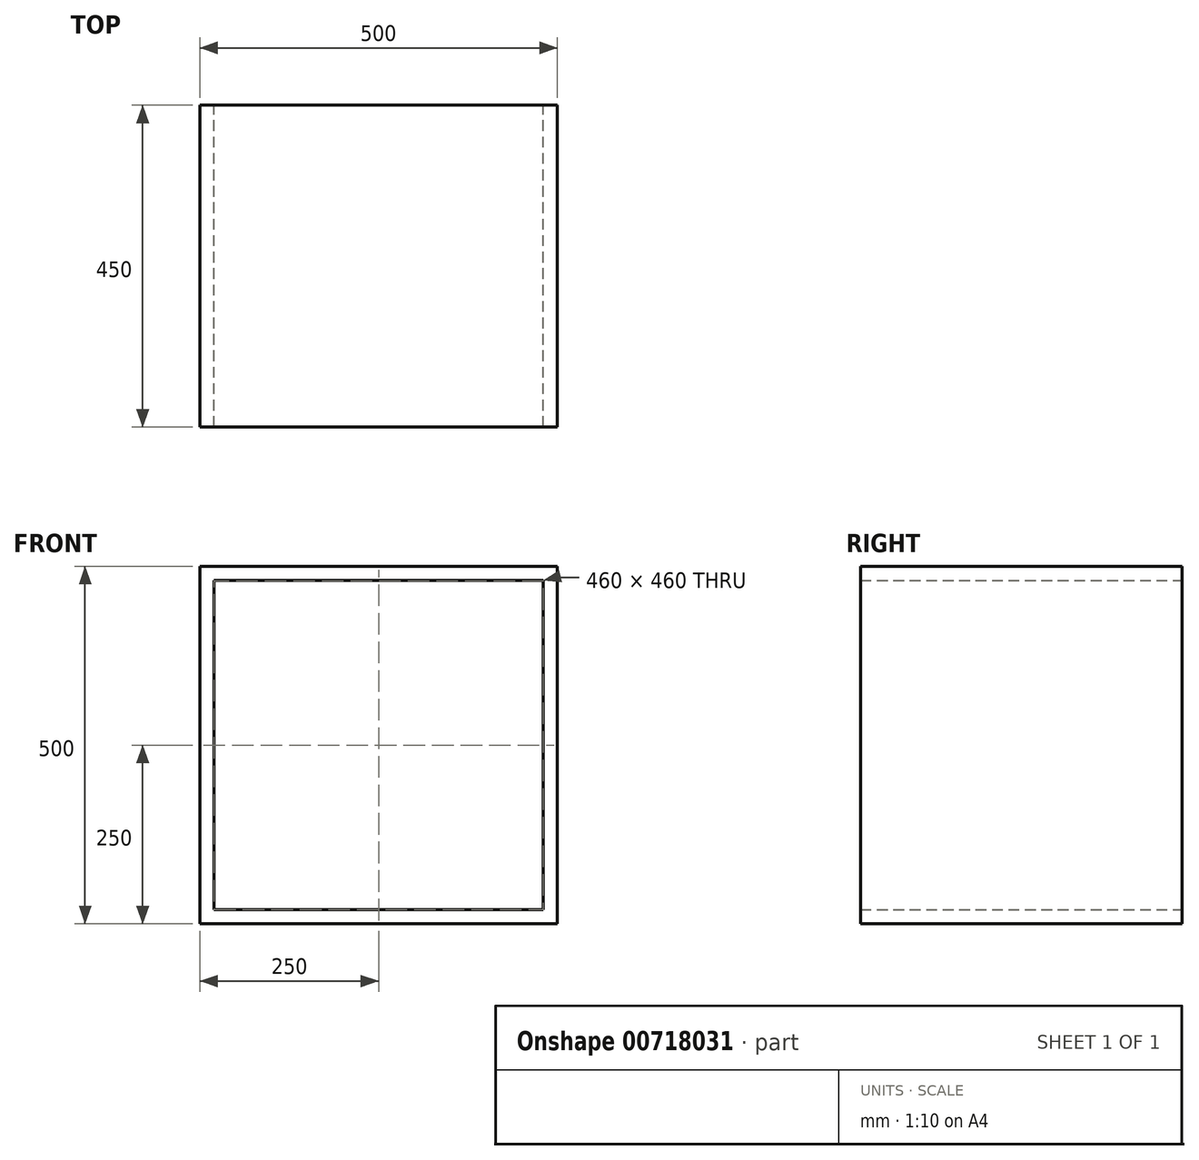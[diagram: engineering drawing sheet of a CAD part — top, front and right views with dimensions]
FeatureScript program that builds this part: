
annotation { "Feature Type Name" : "Feature", "Feature Type Description" : "" }
export const myFeature = defineFeature(function(context is Context, id is Id, definition is map)
    precondition{}
    {
        {
            var Q0;
            Q0=qCreatedBy(makeId("Front.planeOp"),FACE);
            var sketch = newSketch(context, id + "F0", { "sketchPlane" : qUnion([Q0])});
            skLineSegment(sketch, "E0.bottom", {"start": v(250, 250) * mm, "end": v(-250, 250) * mm});
            skLineSegment(sketch, "E0.top", {"start": v(250, -250) * mm, "end": v(-250, -250) * mm});
            skLineSegment(sketch, "E0.left", {"start": v(250, 250) * mm, "end": v(250, -250) * mm});
            skLineSegment(sketch, "E0.right", {"start": v(-250, 250) * mm, "end": v(-250, -250) * mm});
            skPoint(sketch, "E0.middle", {"position": v(0, 0) * mm});
            skLineSegment(sketch, "E1.0", {"start": v(-230, 230) * mm, "end": v(-230, -230) * mm});
            skLineSegment(sketch, "E1.1", {"start": v(230, 230) * mm, "end": v(-230, 230) * mm});
            skLineSegment(sketch, "E1.2", {"start": v(230, 230) * mm, "end": v(230, -230) * mm});
            skLineSegment(sketch, "E1.3", {"start": v(230, -230) * mm, "end": v(-230, -230) * mm});
            skSolve(sketch);
        }
        {
            var Q0;
            Q0=qSketchRegion(id+"F0",true);
            extrude(context, id + "F1", {"entities" : qUnion([Q0]), "depth" : 450 * mm, "offsetDistance" : 25 * mm});
        }
    });
